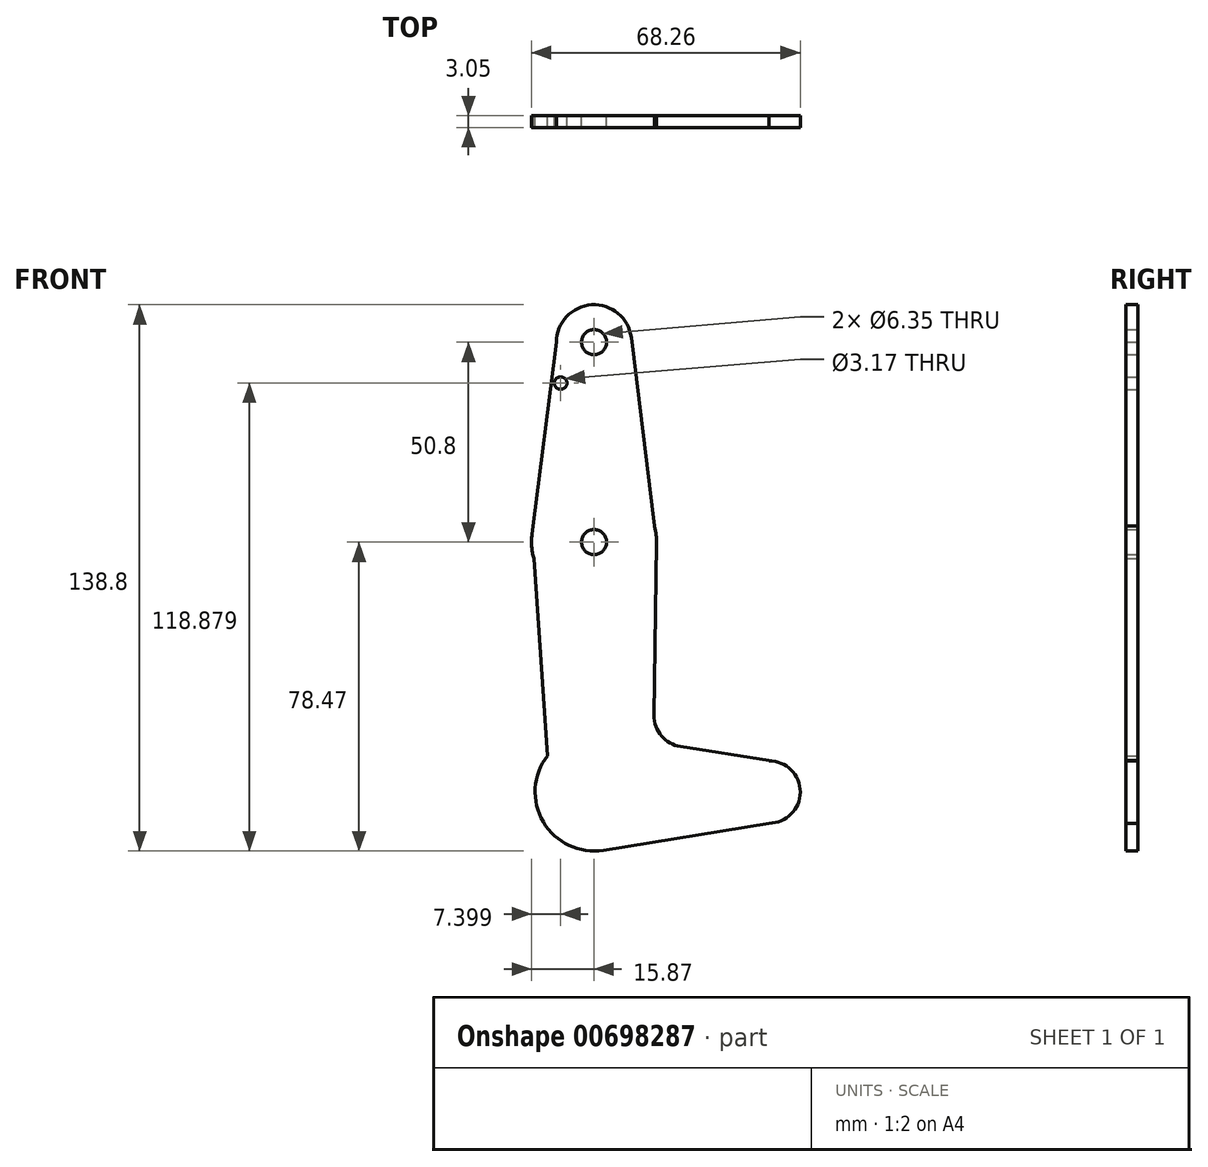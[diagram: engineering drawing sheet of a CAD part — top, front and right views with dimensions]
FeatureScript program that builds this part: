
annotation { "Feature Type Name" : "Feature", "Feature Type Description" : "" }
export const myFeature = defineFeature(function(context is Context, id is Id, definition is map)
    precondition{}
    {
        {
            var Q0;
            Q0=qCreatedBy(makeId("Front.planeOp"),FACE);
            var sketch = newSketch(context, id + "F0", { "sketchPlane" : qUnion([Q0])});
            skLineSegment(sketch, "E0", {"start": v(0, 0) * mm, "end": v(0, 114.3) * mm});
            skLineSegment(sketch, "E1", {"start": v(0, 114.3) * mm, "end": v(0, 0) * mm});
            skCircle(sketch, "E2", {"center": v(0, 63.5) * mm, "radius": 15.88 * mm});
            skCircle(sketch, "E3", {"center": v(0, 114.3) * mm, "radius": 9.53 * mm});
            skPoint(sketch, "E4.center.orphan", {"position": v(-9.53, 114.3) * mm});
            skCircle(sketch, "E5", {"center": v(44.45, 0) * mm, "radius": 7.94 * mm});
            skLineSegment(sketch, "E6", {"start": v(-9.53, 114.3) * mm, "end": v(-15.75, 65.5) * mm});
            skCircle(sketch, "E7", {"center": v(0, 0) * mm, "radius": 14.97 * mm});
            skLineSegment(sketch, "E8", {"start": v(15.25, 19.5) * mm, "end": v(15.87, 63.27) * mm});
            skPoint(sketch, "E8.startSnap0", {"position": v(22.23, 0) * mm});
            skLineSegment(sketch, "E9", {"start": v(15.87, 63.27) * mm, "end": v(9.45, 115.46) * mm});
            skLineSegment(sketch, "E10", {"start": v(9.45, 115.46) * mm, "end": v(15.87, 63.27) * mm});
            skLineSegment(sketch, "E11", {"start": v(15.87, 63.27) * mm, "end": v(-15.75, 65.5) * mm});
            skLineSegment(sketch, "E12", {"start": v(15.87, 63.27) * mm, "end": v(15.35, 67.57) * mm});
            skLineSegment(sketch, "E13", {"start": v(21.97, 11.54) * mm, "end": v(44.45, 8.03) * mm});
            skLineSegment(sketch, "E14", {"start": v(44.45, 8.03) * mm, "end": v(44.45, -7.94) * mm});
            skLineSegment(sketch, "E15", {"start": v(44.45, -7.94) * mm, "end": v(0, -15.17) * mm});
            skLineSegment(sketch, "E16", {"start": v(0, -15.17) * mm, "end": v(44.45, -7.94) * mm});
            skArc(sketch, "E17.filletArc", {"start": v(15.25, 19.5) * mm, "mid": v(17.12, 14.27) * mm, "end": v(21.97, 11.54) * mm});
            skCircle(sketch, "E18", {"center": v(0, 114.3) * mm, "radius": 3.18 * mm});
            skCircle(sketch, "E19", {"center": v(-8.47, 103.9) * mm, "radius": 1.59 * mm});
            skCircle(sketch, "E20", {"center": v(0, 63.5) * mm, "radius": 3.18 * mm});
            skLineSegment(sketch, "E21", {"start": v(-11.78, 9.24) * mm, "end": v(-15.75, 65.5) * mm});
            skSolve(sketch);
        }
        {
            var Q0;
            Q0 = qSketchRegion(id + "F0", true);
            extrude(context, id + "F1", {"entities" : qUnion([Q0]), "depth" : 3.05 * mm, "offsetDistance" : 25.4 * mm});
        }
    });
